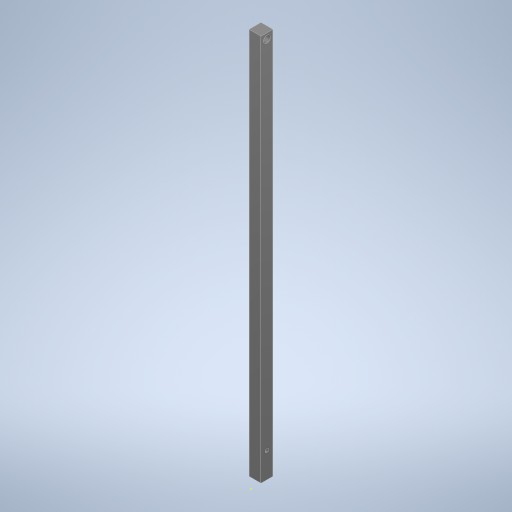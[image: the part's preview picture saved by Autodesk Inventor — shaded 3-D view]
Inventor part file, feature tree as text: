
AUTODESK INVENTOR PART (.ipt)
format: ipt  version: 2024 (Build 280153000, 153)  size: 705,024 bytes
history: native  units: in
note: dims shown in document units (in); Inventor stores cm internally (conversion verified against a paired STEP export)
features: sketch x5, hole x2, extrude x2, imported_body x1
ambient origin geometry x8: Origin, YZ Plane, XZ Plane, XY Plane, X Axis, Y Axis, Z Axis, Center Point
bodies: Solid1 (feature_tree)
feature tree (10):
  imported_body  "Base1"
  hole  "Hole1"  [1 undecoded]
  sketch  "Sketch2"  dims[d2=0.0625in d3=0.75in d4=0.375in d5=0.25in d6=0.5635in d7=1.0in d8=0.8108in d9=0.208in d10=0.0in]
  extrude  "Extrusion1"  Depth=0.208in TaperAngle=0.0deg
  extrude  "Extrusion2"  Depth=0.0984in
  hole  "Hole3"  [1 undecoded]
  sketch  "Sketch1"  dims[d0=0.407in d1=0.0312in]
  sketch  "Sketch3"  dims[d11=2.393in d12=0.0in d13=0.0984in]
  sketch  "Sketch4"  dims[d14=4.2323in d15=0.12in]
  sketch  "Sketch5"  dims[d16=0.12in d24=0.12in d25=0.75in d26=0.375in d27=0.25in d28=0.5635in d29=1.0in d30=0.8108in d17=1.0in d18=1.0in d19=1.0in d20=0.15in d21=0.25in d22=0.375in d23=0.5635in]
note: 2 required parameter values undecoded (feature->parameter linkage not recoverable at this tier; creation-order binding heuristic only, values carry confidence <= 0.55)
